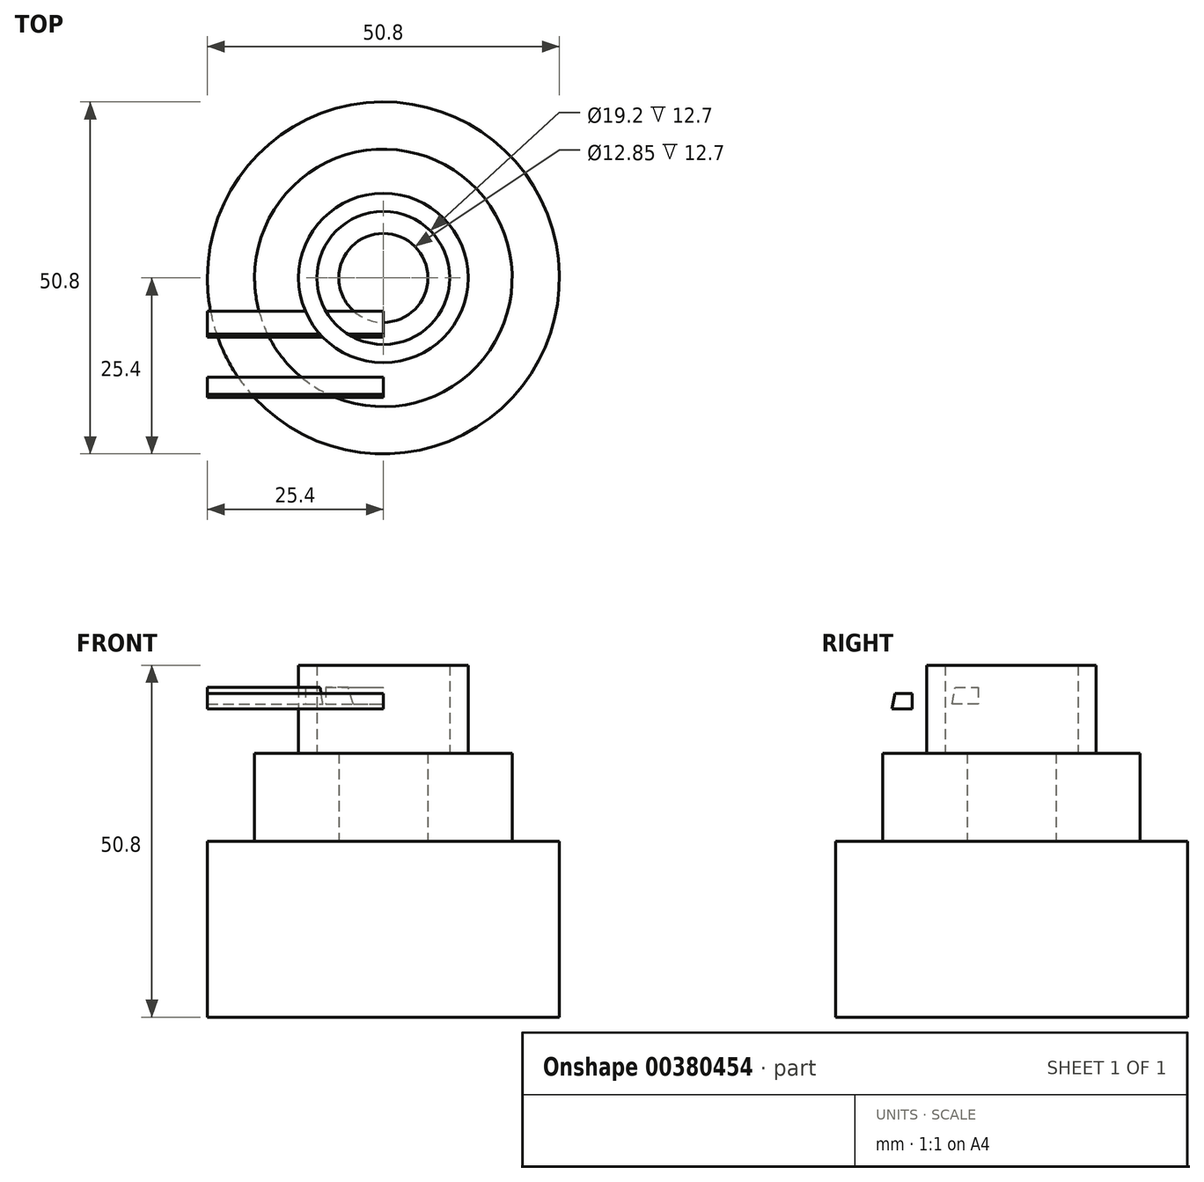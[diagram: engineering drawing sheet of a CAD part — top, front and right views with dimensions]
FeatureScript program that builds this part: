
annotation { "Feature Type Name" : "Feature", "Feature Type Description" : "" }
export const myFeature = defineFeature(function(context is Context, id is Id, definition is map)
    precondition{}
    {
        {
            var Q0;
            Q0=qCreatedBy(makeId("Right.planeOp"),FACE);
            var sketch = newSketch(context, id + "F0", { "sketchPlane" : qUnion([Q0])});
            skLineSegment(sketch, "E0", {"start": v(0, 0) * mm, "end": v(25.4, 0) * mm});
            skLineSegment(sketch, "E1", {"start": v(25.4, 0) * mm, "end": v(25.4, 25.4) * mm});
            skLineSegment(sketch, "E2", {"start": v(25.4, 25.4) * mm, "end": v(0, 25.4) * mm});
            skLineSegment(sketch, "E3", {"start": v(0, 25.4) * mm, "end": v(0, 0) * mm});
            skLineSegment(sketch, "E4", {"start": v(6.81, 25.4) * mm, "end": v(6.81, 38.1) * mm});
            skLineSegment(sketch, "E5", {"start": v(6.81, 38.1) * mm, "end": v(18.97, 38.1) * mm});
            skLineSegment(sketch, "E6", {"start": v(18.97, 38.1) * mm, "end": v(18.97, 25.4) * mm});
            skLineSegment(sketch, "E7", {"start": v(18.97, 25.4) * mm, "end": v(18.97, 38.1) * mm});
            skLineSegment(sketch, "E8", {"start": v(18.97, 38.1) * mm, "end": v(15.8, 38.1) * mm});
            skLineSegment(sketch, "E9", {"start": v(15.8, 38.1) * mm, "end": v(15.8, 50.8) * mm});
            skLineSegment(sketch, "E10", {"start": v(15.8, 50.8) * mm, "end": v(13.16, 50.8) * mm});
            skLineSegment(sketch, "E11", {"start": v(13.16, 50.8) * mm, "end": v(13.16, 38.1) * mm});
            skSolve(sketch);
        }
        {
            var Q0;
            {var subQ0=sQuery(id+"F0.wireOp",EDGE,"E9");Q0=makeQuery(id+"F0.imprint","IMPRINT",FACE,{"disambiguationData":[TD([[makeQuery(id+"F0.imprint","IMPRINT",EDGE,{"derivedFrom":subQ0}),1.0]])]});}
            var Q1;
            {var subQ1=sQuery(id+"F0.wireOp",EDGE,"E4");Q1=makeQuery(id+"F0.imprint","IMPRINT",FACE,{"disambiguationData":[TD([[makeQuery(id+"F0.imprint","IMPRINT",EDGE,{"derivedFrom":subQ1}),-1.0]])]});}
            var Q2;
            Q2=makeQuery(id+"F0.imprint","IMPRINT",FACE,{"disambiguationData":[TD([[makeQuery(id+"F0.imprint","IMPRINT",EDGE,{"derivedFrom":sQuery(id+"F0.wireOp",EDGE,"E0")}),1.0]])]});
            var Q3;
            Q3=sQuery(id+"F0.wireOp",EDGE,"E1");
            revolve(context, id + "F1", {"entities" : qUnion([Q0, Q1, Q2]), "axis" : qUnion([Q3]), "revolveType" : RevolveType.FULL});
        }
        {
            var Q0;
            Q0=qCreatedBy(makeId("Right.planeOp"),FACE);
            var sketch = newSketch(context, id + "F2", { "sketchPlane" : qUnion([Q0])});
            skLineSegment(sketch, "E12", {"start": v(8.61, 46.72) * mm, "end": v(11.05, 46.72) * mm});
            skLineSegment(sketch, "E13", {"start": v(11.05, 46.72) * mm, "end": v(11.05, 44.5) * mm});
            skLineSegment(sketch, "E14", {"start": v(11.05, 44.5) * mm, "end": v(8.17, 44.5) * mm});
            skLineSegment(sketch, "E15", {"start": v(8.17, 44.5) * mm, "end": v(8.61, 46.72) * mm});
            skLineSegment(sketch, "E16", {"start": v(17.27, 47.6) * mm, "end": v(20.6, 47.6) * mm});
            skLineSegment(sketch, "E17", {"start": v(20.6, 47.6) * mm, "end": v(20.6, 45.17) * mm});
            skLineSegment(sketch, "E18", {"start": v(20.6, 45.17) * mm, "end": v(16.82, 45.17) * mm});
            skLineSegment(sketch, "E19", {"start": v(16.82, 45.17) * mm, "end": v(17.27, 47.6) * mm});
            skSolve(sketch);
        }
        {
            var Q0;
            Q0 = qSketchRegion(id + "F2", true);
            extrude(context, id + "F3", {"entities" : qUnion([Q0]), "operationType" : NewBodyOperationType.ADD, "oppositeDirection" : true, "depth" : 25.4 * mm});
        }
    });
